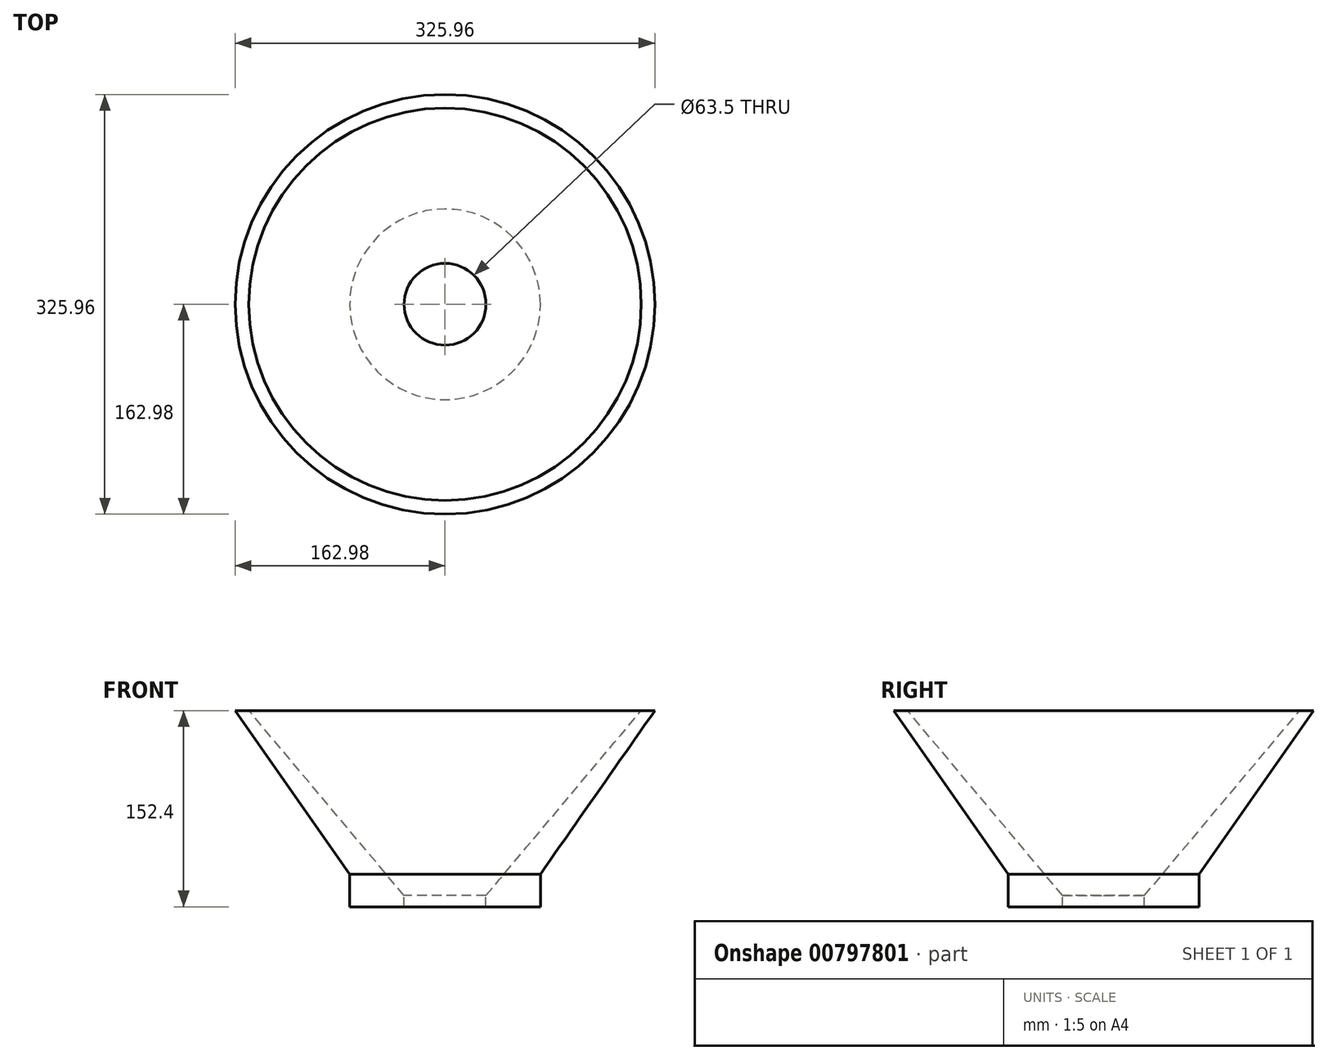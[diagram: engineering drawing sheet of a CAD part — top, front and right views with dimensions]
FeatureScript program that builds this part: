
annotation { "Feature Type Name" : "Feature", "Feature Type Description" : "" }
export const myFeature = defineFeature(function(context is Context, id is Id, definition is map)
    precondition{}
    {
        {
            var Q0;
            Q0=qCreatedBy(makeId("Top.planeOp"),FACE);
            var sketch = newSketch(context, id + "F0", { "sketchPlane" : qUnion([Q0])});
            skCircle(sketch, "E0", {"center": v(0, 0) * mm, "radius": 74.06 * mm});
            skSolve(sketch);
        }
        {
            var Q0;
            Q0 = qSketchRegion(id + "F0", true);
            extrude(context, id + "F1", {"entities" : qUnion([Q0]), "depth" : 127 * mm, "offsetDistance" : 25.4 * mm, "hasDraft" : true, "draftAngle" : 35 * degree, "hasSecondDirection" : true, "secondDirectionOppositeDirection" : true, "secondDirectionDepth" : 25.4 * mm});
        }
        {
            var Q0;
            Q0=makeQuery(id+"F1.opExtrude","CAP_FACE",FACE,{"disambiguationData":[OSD([sQuery(id+"F0.wireOp",EDGE,"E0")])],"isStart":false});
            var sketch = newSketch(context, id + "F2", { "sketchPlane" : qUnion([Q0])});
            skSolve(sketch);
        }
        {
            var Q0;
            Q0=makeQuery(id+"F2.imprint","IMPRINT",FACE,{"disambiguationData":[TD([[makeQuery(id+"F2.imprint","IMPRINT",EDGE,{"derivedFrom":makeQuery(id+"F1.opExtrude","CAP_EDGE",EDGE,{"disambiguationData":[OSD([sQuery(id+"F0.wireOp",EDGE,"E0")])],"isStart":false})}),1.0]])]});
            var sketch = newSketch(context, id + "F3", { "sketchPlane" : qUnion([Q0])});
            skSolve(sketch);
        }
        {
            var Q0;
            Q0=makeQuery(id+"F2.imprint","IMPRINT",FACE,{"disambiguationData":[TD([[makeQuery(id+"F2.imprint","IMPRINT",EDGE,{"derivedFrom":makeQuery(id+"F1.opExtrude","CAP_EDGE",EDGE,{"disambiguationData":[OSD([sQuery(id+"F0.wireOp",EDGE,"E0")])],"isStart":false})}),1.0]])]});
            var sketch = newSketch(context, id + "F4", { "sketchPlane" : qUnion([Q0])});
            skPoint(sketch, "E1", {"position": v(0, 0) * mm});
            skSolve(sketch);
        }
        {
            var Q0;
            Q0=sQuery(id+"F4.wireOp",VERTEX,"E1");
            var Q1;
            Q1=makeQuery(id+"F1.*.split.splitOp","SPLIT",BODY,{"derivedFrom":makeQuery(id+"F1.opExtrude","SWEPT_BODY",BODY,{"disambiguationData":[OSD([sQuery(id+"F0.wireOp",EDGE,"E0")])]})});
            hole(context, id + "F5", {"style" : HoleStyle.C_SINK, "endStyle" : HoleEndStyle.THROUGH, "holeDiameter" : 63.5 * mm, "cSinkDiameter" : 304.8 * mm, "cSinkAngle" : 80 * degree, "majorDiameter" : 6.35 * mm, "isTappedThrough" : true, "tappedDepth" : 12.7 * mm, "tapClearance" : 3, "startFromSketch" : true, "locations" : qUnion([Q0]), "scope" : qUnion([Q1])});
        }
    });
